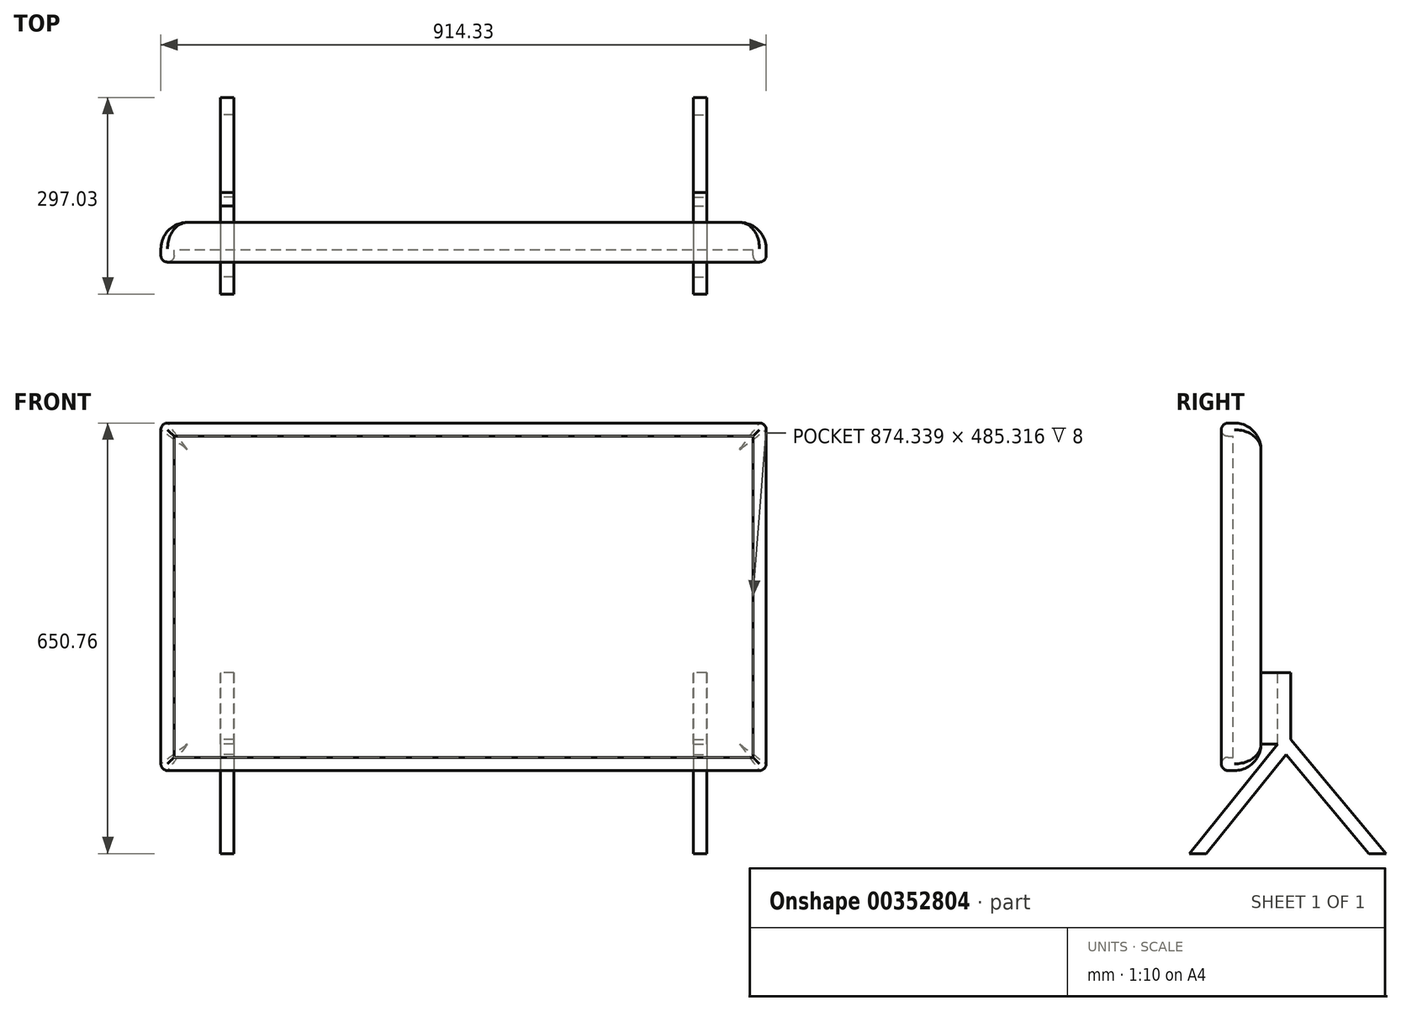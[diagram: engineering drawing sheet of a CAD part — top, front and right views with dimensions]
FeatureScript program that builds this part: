
annotation { "Feature Type Name" : "Feature", "Feature Type Description" : "" }
export const myFeature = defineFeature(function(context is Context, id is Id, definition is map)
    precondition{}
    {
        {
            var Q0;
            Q0=qCreatedBy(makeId("Front.planeOp"),FACE);
            var sketch = newSketch(context, id + "F0", { "sketchPlane" : qUnion([Q0])});
            skLineSegment(sketch, "E0.bottom", {"start": v(-389.41, 197.16) * mm, "end": v(484.92, 197.16) * mm});
            skLineSegment(sketch, "E0.top", {"start": v(-389.41, -288.16) * mm, "end": v(484.92, -288.16) * mm});
            skLineSegment(sketch, "E0.left", {"start": v(-389.41, 197.16) * mm, "end": v(-389.41, -288.16) * mm});
            skLineSegment(sketch, "E0.right", {"start": v(484.92, 197.16) * mm, "end": v(484.92, -288.16) * mm});
            skLineSegment(sketch, "E1", {"start": v(-389.41, 197.16) * mm, "end": v(484.92, -288.16) * mm});
            skLineSegment(sketch, "E2.0", {"start": v(-409.41, 217.16) * mm, "end": v(504.92, 217.16) * mm});
            skLineSegment(sketch, "E2.1", {"start": v(-409.41, 217.16) * mm, "end": v(-409.41, -308.16) * mm});
            skLineSegment(sketch, "E2.2", {"start": v(-409.41, -308.16) * mm, "end": v(504.92, -308.16) * mm});
            skLineSegment(sketch, "E2.3", {"start": v(504.92, 217.16) * mm, "end": v(504.92, -308.16) * mm});
            skSolve(sketch);
        }
        {
            var Q0;
            Q0 = qSketchRegion(id + "F0", true);
            extrude(context, id + "F1", {"entities" : qUnion([Q0]), "depth" : 60 * mm});
        }
        {
            var Q0;
            Q0=makeQuery(id+"F1.opExtrude","CAP_FACE",FACE,{"disambiguationData":[OSD([sQuery(id+"F0.wireOp",EDGE,"E0.bottom"),sQuery(id+"F0.wireOp",EDGE,"E0.top"),sQuery(id+"F0.wireOp",EDGE,"E0.left"),sQuery(id+"F0.wireOp",EDGE,"E0.right"),sQuery(id+"F0.wireOp",EDGE,"E2.0"),sQuery(id+"F0.wireOp",EDGE,"E2.1"),sQuery(id+"F0.wireOp",EDGE,"E2.2"),sQuery(id+"F0.wireOp",EDGE,"E2.3")])],"isStart":false});
            var Q1;
            Q1=makeQuery(id+"F1.opExtrude","SWEPT_EDGE",EDGE,{"disambiguationData":[OSD([sQuery(id+"F0.wireOp",EDGE,"E2.0"),sQuery(id+"F0.wireOp",EDGE,"E2.3")])]});
            var Q2;
            Q2=makeQuery(id+"F1.opExtrude","SWEPT_EDGE",EDGE,{"disambiguationData":[OSD([sQuery(id+"F0.wireOp",EDGE,"E2.2"),sQuery(id+"F0.wireOp",EDGE,"E2.3")])]});
            var Q3;
            Q3=makeQuery(id+"F1.opExtrude","SWEPT_EDGE",EDGE,{"disambiguationData":[OSD([sQuery(id+"F0.wireOp",EDGE,"E2.1"),sQuery(id+"F0.wireOp",EDGE,"E2.2")])]});
            var Q4;
            Q4=makeQuery(id+"F1.opExtrude","SWEPT_EDGE",EDGE,{"disambiguationData":[OSD([sQuery(id+"F0.wireOp",EDGE,"E2.0"),sQuery(id+"F0.wireOp",EDGE,"E2.1")])]});
            fillet(context, id + "F2", {"entities" : qUnion([Q0, Q1, Q2, Q3, Q4]), "radius" : 10 * mm, "tangentPropagation" : true, "allowEdgeOverflow" : false});
        }
        {
            var Q0;
            Q0=makeQuery(id+"F1.opExtrude","CAP_FACE",FACE,{"disambiguationData":[OSD([sQuery(id+"F0.wireOp",EDGE,"E0.bottom"),sQuery(id+"F0.wireOp",EDGE,"E0.top"),sQuery(id+"F0.wireOp",EDGE,"E0.left"),sQuery(id+"F0.wireOp",EDGE,"E0.right"),sQuery(id+"F0.wireOp",EDGE,"E2.0"),sQuery(id+"F0.wireOp",EDGE,"E2.1"),sQuery(id+"F0.wireOp",EDGE,"E2.2"),sQuery(id+"F0.wireOp",EDGE,"E2.3")])],"isStart":true});
            var sketch = newSketch(context, id + "F3", { "sketchPlane" : qUnion([Q0])});
            skLineSegment(sketch, "E3.0", {"start": v(399.41, 217.16) * mm, "end": v(-494.92, 217.16) * mm});
            skArc(sketch, "E4.0", {"start": v(-494.92, 217.16) * mm, "mid": v(-502, 214.23) * mm, "end": v(-504.92, 207.16) * mm});
            skLineSegment(sketch, "E5.0", {"start": v(-504.92, 207.16) * mm, "end": v(-504.92, -298.16) * mm});
            skArc(sketch, "E6.0", {"start": v(-504.92, -298.16) * mm, "mid": v(-502, -305.23) * mm, "end": v(-494.92, -308.16) * mm});
            skLineSegment(sketch, "E7.0", {"start": v(399.41, -308.16) * mm, "end": v(-494.92, -308.16) * mm});
            skArc(sketch, "E8.0", {"start": v(399.41, -308.16) * mm, "mid": v(406.49, -305.23) * mm, "end": v(409.41, -298.16) * mm});
            skLineSegment(sketch, "E9.0", {"start": v(409.41, 207.16) * mm, "end": v(409.41, -298.16) * mm});
            skArc(sketch, "E10.0", {"start": v(409.41, 207.16) * mm, "mid": v(406.49, 214.23) * mm, "end": v(399.41, 217.16) * mm});
            skSolve(sketch);
        }
        {
            var Q0;
            Q0 = qSketchRegion(id + "F3", true);
            extrude(context, id + "F4", {"entities" : qUnion([Q0]), "operationType" : NewBodyOperationType.ADD, "oppositeDirection" : true, "depth" : 42 * mm});
        }
        {
            var Q0;
            Q0=makeQuery(id+"F4.boolean.opBoolean","MERGE",FACE,{"derivedFrom":[makeQuery(id+"F1.opExtrude","CAP_FACE",FACE,{"disambiguationData":[OSD([sQuery(id+"F0.wireOp",EDGE,"E0.bottom"),sQuery(id+"F0.wireOp",EDGE,"E0.top"),sQuery(id+"F0.wireOp",EDGE,"E0.left"),sQuery(id+"F0.wireOp",EDGE,"E0.right"),sQuery(id+"F0.wireOp",EDGE,"E2.0"),sQuery(id+"F0.wireOp",EDGE,"E2.1"),sQuery(id+"F0.wireOp",EDGE,"E2.2"),sQuery(id+"F0.wireOp",EDGE,"E2.3")])],"isStart":true}),makeQuery(id+"F4.opExtrude","CAP_FACE",FACE,{"disambiguationData":[OSD([sQuery(id+"F3.wireOp",EDGE,"E3.0"),sQuery(id+"F3.wireOp",EDGE,"E4.0"),sQuery(id+"F3.wireOp",EDGE,"E5.0"),sQuery(id+"F3.wireOp",EDGE,"E6.0"),sQuery(id+"F3.wireOp",EDGE,"E7.0"),sQuery(id+"F3.wireOp",EDGE,"E8.0"),sQuery(id+"F3.wireOp",EDGE,"E9.0"),sQuery(id+"F3.wireOp",EDGE,"E10.0")])],"isStart":true})]});
            fillet(context, id + "F5", {"entities" : qUnion([Q0]), "radius" : 40 * mm, "tangentPropagation" : true, "allowEdgeOverflow" : false});
        }
        {
            var Q0;
            Q0=makeQuery(id+"F4.boolean.opBoolean","MERGE",FACE,{"derivedFrom":[makeQuery(id+"F1.opExtrude","CAP_FACE",FACE,{"disambiguationData":[OSD([sQuery(id+"F0.wireOp",EDGE,"E0.bottom"),sQuery(id+"F0.wireOp",EDGE,"E0.top"),sQuery(id+"F0.wireOp",EDGE,"E0.left"),sQuery(id+"F0.wireOp",EDGE,"E0.right"),sQuery(id+"F0.wireOp",EDGE,"E2.0"),sQuery(id+"F0.wireOp",EDGE,"E2.1"),sQuery(id+"F0.wireOp",EDGE,"E2.2"),sQuery(id+"F0.wireOp",EDGE,"E2.3")])],"isStart":true}),makeQuery(id+"F4.opExtrude","CAP_FACE",FACE,{"disambiguationData":[OSD([sQuery(id+"F3.wireOp",EDGE,"E3.0"),sQuery(id+"F3.wireOp",EDGE,"E4.0"),sQuery(id+"F3.wireOp",EDGE,"E5.0"),sQuery(id+"F3.wireOp",EDGE,"E6.0"),sQuery(id+"F3.wireOp",EDGE,"E7.0"),sQuery(id+"F3.wireOp",EDGE,"E8.0"),sQuery(id+"F3.wireOp",EDGE,"E9.0"),sQuery(id+"F3.wireOp",EDGE,"E10.0")])],"isStart":true})]});
            var sketch = newSketch(context, id + "F6", { "sketchPlane" : qUnion([Q0])});
            skLineSegment(sketch, "E11", {"start": v(-464.92, -268.16) * mm, "end": v(-414.92, -268.16) * mm});
            skLineSegment(sketch, "E12", {"start": v(369.41, -268.16) * mm, "end": v(319.41, -268.16) * mm});
            skLineSegment(sketch, "E13.bottom", {"start": v(-414.92, -268.16) * mm, "end": v(-394.92, -268.16) * mm});
            skLineSegment(sketch, "E13.top", {"start": v(-414.92, -160.29) * mm, "end": v(-394.92, -160.29) * mm});
            skLineSegment(sketch, "E13.left", {"start": v(-414.92, -268.16) * mm, "end": v(-414.92, -160.29) * mm});
            skLineSegment(sketch, "E13.right", {"start": v(-394.92, -268.16) * mm, "end": v(-394.92, -160.29) * mm});
            skLineSegment(sketch, "E14.bottom", {"start": v(319.41, -268.16) * mm, "end": v(299.41, -268.16) * mm});
            skLineSegment(sketch, "E14.top", {"start": v(319.41, -160.29) * mm, "end": v(299.41, -160.29) * mm});
            skLineSegment(sketch, "E14.left", {"start": v(319.41, -268.16) * mm, "end": v(319.41, -160.29) * mm});
            skLineSegment(sketch, "E14.right", {"start": v(299.41, -268.16) * mm, "end": v(299.41, -160.29) * mm});
            skSolve(sketch);
        }
        {
            var Q0;
            Q0 = qSketchRegion(id + "F6", true);
            extrude(context, id + "F7", {"entities" : qUnion([Q0]), "operationType" : NewBodyOperationType.ADD, "depth" : 25 * mm});
        }
        {
            var Q0;
            Q0=makeQuery(id+"F7.opExtrude","SWEPT_FACE",FACE,{"disambiguationData":[OSD([sQuery(id+"F6.wireOp",EDGE,"E13.left")])]});
            var sketch = newSketch(context, id + "F8", { "sketchPlane" : qUnion([Q0])});
            skLineSegment(sketch, "E15", {"start": v(25, -160.29) * mm, "end": v(25, -268.16) * mm});
            skLineSegment(sketch, "E16", {"start": v(25, -268.16) * mm, "end": v(-108.34, -433.6) * mm});
            skLineSegment(sketch, "E17", {"start": v(-108.34, -433.6) * mm, "end": v(-82.65, -433.6) * mm});
            skLineSegment(sketch, "E18.0", {"start": v(38.05, -283.84) * mm, "end": v(-82.65, -433.6) * mm});
            skLineSegment(sketch, "E18.1", {"start": v(45, -160.29) * mm, "end": v(45, -260.93) * mm});
            skLineSegment(sketch, "E19", {"start": v(38.05, -283.84) * mm, "end": v(162.67, -433.6) * mm});
            skLineSegment(sketch, "E20.0", {"start": v(45, -260.93) * mm, "end": v(178.04, -420.81) * mm});
            skLineSegment(sketch, "E21", {"start": v(162.67, -433.6) * mm, "end": v(188.69, -433.6) * mm});
            skLineSegment(sketch, "E22", {"start": v(178.04, -420.81) * mm, "end": v(188.69, -433.6) * mm});
            skLineSegment(sketch, "E23", {"start": v(25, -160.29) * mm, "end": v(45, -160.29) * mm});
            skSolve(sketch);
        }
        {
            var Q0;
            Q0=makeQuery(id+"F8.imprint","IMPRINT",FACE,{"disambiguationData":[TD([[makeQuery(id+"F8.imprint","IMPRINT",EDGE,{"derivedFrom":sQuery(id+"F8.wireOp",EDGE,"E15")}),-1.0]])]});
            extrude(context, id + "F9", {"entities" : qUnion([Q0]), "operationType" : NewBodyOperationType.ADD, "oppositeDirection" : true, "depth" : 20 * mm});
        }
        {
            var Q0;
            Q0=makeQuery(id+"F7.opExtrude","SWEPT_FACE",FACE,{"disambiguationData":[OSD([sQuery(id+"F6.wireOp",EDGE,"E14.left")])]});
            var sketch = newSketch(context, id + "F10", { "sketchPlane" : qUnion([Q0])});
            skLineSegment(sketch, "E24.0", {"start": v(-38.05, -283.84) * mm, "end": v(-162.67, -433.6) * mm});
            skLineSegment(sketch, "E25.0", {"start": v(-38.05, -283.84) * mm, "end": v(82.65, -433.6) * mm});
            skLineSegment(sketch, "E26.0", {"start": v(-25, -268.16) * mm, "end": v(108.34, -433.6) * mm});
            skLineSegment(sketch, "E27.0", {"start": v(-45, -260.93) * mm, "end": v(-188.69, -433.6) * mm});
            skLineSegment(sketch, "E28.0", {"start": v(-45, -160.29) * mm, "end": v(-45, -260.93) * mm});
            skLineSegment(sketch, "E29", {"start": v(-188.69, -433.6) * mm, "end": v(-162.67, -433.6) * mm});
            skLineSegment(sketch, "E30", {"start": v(82.65, -433.6) * mm, "end": v(108.34, -433.6) * mm});
            skLineSegment(sketch, "E31", {"start": v(-25, -160.29) * mm, "end": v(-45, -160.29) * mm});
            skLineSegment(sketch, "E32", {"start": v(-25, -160.29) * mm, "end": v(0, -160.29) * mm});
            skLineSegment(sketch, "E33", {"start": v(0, -160.29) * mm, "end": v(0, -268.16) * mm});
            skLineSegment(sketch, "E34", {"start": v(0, -268.16) * mm, "end": v(-25, -268.16) * mm});
            skSolve(sketch);
        }
        {
            var Q0;
            Q0 = qSketchRegion(id + "F10", true);
            extrude(context, id + "F11", {"entities" : qUnion([Q0]), "oppositeDirection" : true, "depth" : 20 * mm});
        }
        {
            var Q0;
            Q0 = qSketchRegion(id + "F10", true);
            extrude(context, id + "F12", {"entities" : qUnion([Q0]), "oppositeDirection" : true, "depth" : 20 * mm});
        }
    });
